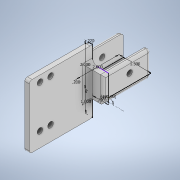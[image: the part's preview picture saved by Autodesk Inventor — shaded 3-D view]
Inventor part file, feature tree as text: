
AUTODESK INVENTOR PART (.ipt)
format: ipt  version: 2020 (Build 240168000, 168)  size: 211,968 bytes
history: native  units: in
note: dims shown in document units (in); Inventor stores cm internally (conversion verified against a paired STEP export)
features: sketch x4, extrude x4, fillet x4, hole x2
ambient origin geometry x8: Origin, YZ Plane, XZ Plane, XY Plane, X Axis, Y Axis, Z Axis, Center Point
bodies: Solid1 (feature_tree)
feature tree (14):
  sketch  "Sketch1"  dims[d0=1.5in d1=2.0in]
  extrude  "Extrusion1"  Depth=2.0in
  extrude  "Extrusion2"  Depth=0.2in
  hole  "Hole1"  [1 undecoded]
  sketch  "Sketch3"  dims[d4=1.0in d5=0.0in d6=0.2in d7=0.0in]
  extrude  "Extrusion3"  Depth=0.75in
  extrude  "Extrusion4"  TaperAngle=180.0deg  [1 undecoded]
  hole  "Hole2"  [1 undecoded]
  fillet  "Fillet1"  Radius=2.0in
  fillet  "Fillet2"  Radius=1.0in
  fillet  "Fillet3"  Radius=0.25in
  fillet  "Fillet4"  Radius=3.0in
  sketch  "Sketch2"  dims[d2=0.2in d3=0.2in]
  sketch  "Sketch4"  dims[d8=0.5in d9=0.266in d10=0.75in d11=0.438in d12=0.25in d13=0.5635in d14=1.0in d15=0.8108in d16=0.75in d17=180.0deg d18=0.22in d19=2.0in d20=1.0in d21=0.25in d22=0.0in d23=3.0in d24=0.0in d25=0.5in d26=0.0in d27=0.5in d28=0.5in d29=2.0in d30=0.266in d31=0.75in d32=0.438in d33=0.25in d34=0.5635in d35=0.95in d36=0.8108in d37=0.25in d38=0.125in d39=0.25in d40=0.125in]
note: 3 required parameter values undecoded (feature->parameter linkage not recoverable at this tier; creation-order binding heuristic only, values carry confidence <= 0.55)
